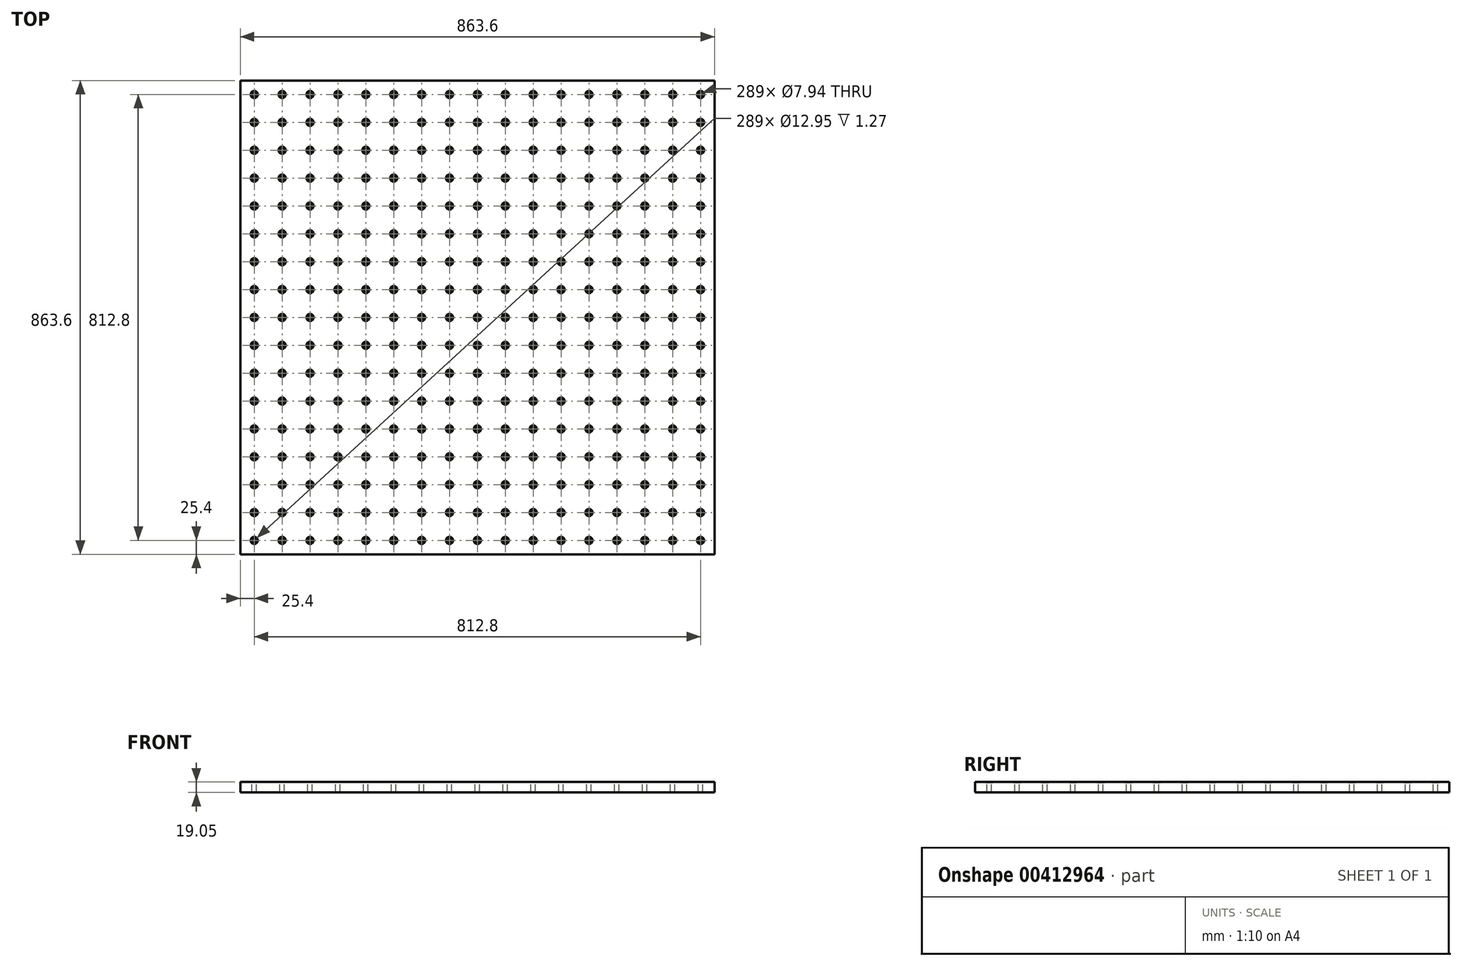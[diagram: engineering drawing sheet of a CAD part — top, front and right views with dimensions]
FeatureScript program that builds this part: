
annotation { "Feature Type Name" : "Feature", "Feature Type Description" : "" }
export const myFeature = defineFeature(function(context is Context, id is Id, definition is map)
    precondition{}
    {
        {
            var Q0;
            Q0=qCreatedBy(makeId("Top.planeOp"),FACE);
            var sketch = newSketch(context, id + "F0", { "sketchPlane" : qUnion([Q0])});
            skLineSegment(sketch, "E0.bottom", {"start": v(431.8, -431.8) * mm, "end": v(-431.8, -431.8) * mm});
            skLineSegment(sketch, "E0.top", {"start": v(431.8, 431.8) * mm, "end": v(-431.8, 431.8) * mm});
            skLineSegment(sketch, "E0.left", {"start": v(431.8, -431.8) * mm, "end": v(431.8, 431.8) * mm});
            skLineSegment(sketch, "E0.right", {"start": v(-431.8, -431.8) * mm, "end": v(-431.8, 431.8) * mm});
            skPoint(sketch, "E0.middle", {"position": v(0, 0) * mm});
            skSolve(sketch);
        }
        {
            var Q0;
            Q0=makeQuery(id+"F0.imprint","IMPRINT",FACE,{"disambiguationData":[TD([[makeQuery(id+"F0.imprint","IMPRINT",EDGE,{"derivedFrom":sQuery(id+"F0.wireOp",EDGE,"E0.bottom")}),-1.0]])]});
            extrude(context, id + "F1", {"entities" : qUnion([Q0]), "depth" : 19.05 * mm});
        }
        {
            var Q0;
            Q0=makeQuery(id+"F1.opExtrude","CAP_FACE",FACE,{"disambiguationData":[OSD([sQuery(id+"F0.wireOp",EDGE,"E0.bottom"),sQuery(id+"F0.wireOp",EDGE,"E0.top"),sQuery(id+"F0.wireOp",EDGE,"E0.left"),sQuery(id+"F0.wireOp",EDGE,"E0.right")])],"isStart":false});
            var sketch = newSketch(context, id + "F2", { "sketchPlane" : qUnion([Q0])});
            skLineSegment(sketch, "E1.bottom", {"start": v(406.4, -406.4) * mm, "end": v(-406.4, -406.4) * mm, "construction": true});
            skLineSegment(sketch, "E1.top", {"start": v(406.4, 406.4) * mm, "end": v(-406.4, 406.4) * mm, "construction": true});
            skLineSegment(sketch, "E1.left", {"start": v(406.4, -406.4) * mm, "end": v(406.4, 406.4) * mm, "construction": true});
            skLineSegment(sketch, "E1.right", {"start": v(-406.4, -406.4) * mm, "end": v(-406.4, 406.4) * mm, "construction": true});
            skPoint(sketch, "E1.middle", {"position": v(0, 0) * mm});
            skPoint(sketch, "E2", {"position": v(-406.4, -406.4) * mm});
            skPoint(sketch, "E3.0.1.0", {"position": v(-406.4, -355.6) * mm});
            skPoint(sketch, "E3.0.2.0", {"position": v(-406.4, -304.8) * mm});
            skPoint(sketch, "E3.0.3.0", {"position": v(-406.4, -254) * mm});
            skPoint(sketch, "E3.0.4.0", {"position": v(-406.4, -203.2) * mm});
            skPoint(sketch, "E3.0.5.0", {"position": v(-406.4, -152.4) * mm});
            skPoint(sketch, "E3.0.6.0", {"position": v(-406.4, -101.6) * mm});
            skPoint(sketch, "E3.0.7.0", {"position": v(-406.4, -50.8) * mm});
            skPoint(sketch, "E3.0.8.0", {"position": v(-406.4, 0) * mm});
            skPoint(sketch, "E3.0.9.0", {"position": v(-406.4, 50.8) * mm});
            skPoint(sketch, "E3.0.10.0", {"position": v(-406.4, 101.6) * mm});
            skPoint(sketch, "E3.0.11.0", {"position": v(-406.4, 152.4) * mm});
            skPoint(sketch, "E3.0.12.0", {"position": v(-406.4, 203.2) * mm});
            skPoint(sketch, "E3.0.13.0", {"position": v(-406.4, 254) * mm});
            skPoint(sketch, "E3.0.14.0", {"position": v(-406.4, 304.8) * mm});
            skPoint(sketch, "E3.0.15.0", {"position": v(-406.4, 355.6) * mm});
            skPoint(sketch, "E3.0.16.0", {"position": v(-406.4, 406.4) * mm});
            skPoint(sketch, "E3.1.0.0", {"position": v(-355.6, -406.4) * mm});
            skPoint(sketch, "E3.1.1.0", {"position": v(-355.6, -355.6) * mm});
            skPoint(sketch, "E3.1.2.0", {"position": v(-355.6, -304.8) * mm});
            skPoint(sketch, "E3.1.3.0", {"position": v(-355.6, -254) * mm});
            skPoint(sketch, "E3.1.4.0", {"position": v(-355.6, -203.2) * mm});
            skPoint(sketch, "E3.1.5.0", {"position": v(-355.6, -152.4) * mm});
            skPoint(sketch, "E3.1.6.0", {"position": v(-355.6, -101.6) * mm});
            skPoint(sketch, "E3.1.7.0", {"position": v(-355.6, -50.8) * mm});
            skPoint(sketch, "E3.1.8.0", {"position": v(-355.6, 0) * mm});
            skPoint(sketch, "E3.1.9.0", {"position": v(-355.6, 50.8) * mm});
            skPoint(sketch, "E3.1.10.0", {"position": v(-355.6, 101.6) * mm});
            skPoint(sketch, "E3.1.11.0", {"position": v(-355.6, 152.4) * mm});
            skPoint(sketch, "E3.1.12.0", {"position": v(-355.6, 203.2) * mm});
            skPoint(sketch, "E3.1.13.0", {"position": v(-355.6, 254) * mm});
            skPoint(sketch, "E3.1.14.0", {"position": v(-355.6, 304.8) * mm});
            skPoint(sketch, "E3.1.15.0", {"position": v(-355.6, 355.6) * mm});
            skPoint(sketch, "E3.1.16.0", {"position": v(-355.6, 406.4) * mm});
            skPoint(sketch, "E3.2.0.0", {"position": v(-304.8, -406.4) * mm});
            skPoint(sketch, "E3.2.1.0", {"position": v(-304.8, -355.6) * mm});
            skPoint(sketch, "E3.2.2.0", {"position": v(-304.8, -304.8) * mm});
            skPoint(sketch, "E3.2.3.0", {"position": v(-304.8, -254) * mm});
            skPoint(sketch, "E3.2.4.0", {"position": v(-304.8, -203.2) * mm});
            skPoint(sketch, "E3.2.5.0", {"position": v(-304.8, -152.4) * mm});
            skPoint(sketch, "E3.2.6.0", {"position": v(-304.8, -101.6) * mm});
            skPoint(sketch, "E3.2.7.0", {"position": v(-304.8, -50.8) * mm});
            skPoint(sketch, "E3.2.8.0", {"position": v(-304.8, 0) * mm});
            skPoint(sketch, "E3.2.9.0", {"position": v(-304.8, 50.8) * mm});
            skPoint(sketch, "E3.2.10.0", {"position": v(-304.8, 101.6) * mm});
            skPoint(sketch, "E3.2.11.0", {"position": v(-304.8, 152.4) * mm});
            skPoint(sketch, "E3.2.12.0", {"position": v(-304.8, 203.2) * mm});
            skPoint(sketch, "E3.2.13.0", {"position": v(-304.8, 254) * mm});
            skPoint(sketch, "E3.2.14.0", {"position": v(-304.8, 304.8) * mm});
            skPoint(sketch, "E3.2.15.0", {"position": v(-304.8, 355.6) * mm});
            skPoint(sketch, "E3.2.16.0", {"position": v(-304.8, 406.4) * mm});
            skPoint(sketch, "E3.3.0.0", {"position": v(-254, -406.4) * mm});
            skPoint(sketch, "E3.3.1.0", {"position": v(-254, -355.6) * mm});
            skPoint(sketch, "E3.3.2.0", {"position": v(-254, -304.8) * mm});
            skPoint(sketch, "E3.3.3.0", {"position": v(-254, -254) * mm});
            skPoint(sketch, "E3.3.4.0", {"position": v(-254, -203.2) * mm});
            skPoint(sketch, "E3.3.5.0", {"position": v(-254, -152.4) * mm});
            skPoint(sketch, "E3.3.6.0", {"position": v(-254, -101.6) * mm});
            skPoint(sketch, "E3.3.7.0", {"position": v(-254, -50.8) * mm});
            skPoint(sketch, "E3.3.8.0", {"position": v(-254, 0) * mm});
            skPoint(sketch, "E3.3.9.0", {"position": v(-254, 50.8) * mm});
            skPoint(sketch, "E3.3.10.0", {"position": v(-254, 101.6) * mm});
            skPoint(sketch, "E3.3.11.0", {"position": v(-254, 152.4) * mm});
            skPoint(sketch, "E3.3.12.0", {"position": v(-254, 203.2) * mm});
            skPoint(sketch, "E3.3.13.0", {"position": v(-254, 254) * mm});
            skPoint(sketch, "E3.3.14.0", {"position": v(-254, 304.8) * mm});
            skPoint(sketch, "E3.3.15.0", {"position": v(-254, 355.6) * mm});
            skPoint(sketch, "E3.3.16.0", {"position": v(-254, 406.4) * mm});
            skPoint(sketch, "E3.4.0.0", {"position": v(-203.2, -406.4) * mm});
            skPoint(sketch, "E3.4.1.0", {"position": v(-203.2, -355.6) * mm});
            skPoint(sketch, "E3.4.2.0", {"position": v(-203.2, -304.8) * mm});
            skPoint(sketch, "E3.4.3.0", {"position": v(-203.2, -254) * mm});
            skPoint(sketch, "E3.4.4.0", {"position": v(-203.2, -203.2) * mm});
            skPoint(sketch, "E3.4.5.0", {"position": v(-203.2, -152.4) * mm});
            skPoint(sketch, "E3.4.6.0", {"position": v(-203.2, -101.6) * mm});
            skPoint(sketch, "E3.4.7.0", {"position": v(-203.2, -50.8) * mm});
            skPoint(sketch, "E3.4.8.0", {"position": v(-203.2, 0) * mm});
            skPoint(sketch, "E3.4.9.0", {"position": v(-203.2, 50.8) * mm});
            skPoint(sketch, "E3.4.10.0", {"position": v(-203.2, 101.6) * mm});
            skPoint(sketch, "E3.4.11.0", {"position": v(-203.2, 152.4) * mm});
            skPoint(sketch, "E3.4.12.0", {"position": v(-203.2, 203.2) * mm});
            skPoint(sketch, "E3.4.13.0", {"position": v(-203.2, 254) * mm});
            skPoint(sketch, "E3.4.14.0", {"position": v(-203.2, 304.8) * mm});
            skPoint(sketch, "E3.4.15.0", {"position": v(-203.2, 355.6) * mm});
            skPoint(sketch, "E3.4.16.0", {"position": v(-203.2, 406.4) * mm});
            skPoint(sketch, "E3.5.0.0", {"position": v(-152.4, -406.4) * mm});
            skPoint(sketch, "E3.5.1.0", {"position": v(-152.4, -355.6) * mm});
            skPoint(sketch, "E3.5.2.0", {"position": v(-152.4, -304.8) * mm});
            skPoint(sketch, "E3.5.3.0", {"position": v(-152.4, -254) * mm});
            skPoint(sketch, "E3.5.4.0", {"position": v(-152.4, -203.2) * mm});
            skPoint(sketch, "E3.5.5.0", {"position": v(-152.4, -152.4) * mm});
            skPoint(sketch, "E3.5.6.0", {"position": v(-152.4, -101.6) * mm});
            skPoint(sketch, "E3.5.7.0", {"position": v(-152.4, -50.8) * mm});
            skPoint(sketch, "E3.5.8.0", {"position": v(-152.4, 0) * mm});
            skPoint(sketch, "E3.5.9.0", {"position": v(-152.4, 50.8) * mm});
            skPoint(sketch, "E3.5.10.0", {"position": v(-152.4, 101.6) * mm});
            skPoint(sketch, "E3.5.11.0", {"position": v(-152.4, 152.4) * mm});
            skPoint(sketch, "E3.5.12.0", {"position": v(-152.4, 203.2) * mm});
            skPoint(sketch, "E3.5.13.0", {"position": v(-152.4, 254) * mm});
            skPoint(sketch, "E3.5.14.0", {"position": v(-152.4, 304.8) * mm});
            skPoint(sketch, "E3.5.15.0", {"position": v(-152.4, 355.6) * mm});
            skPoint(sketch, "E3.5.16.0", {"position": v(-152.4, 406.4) * mm});
            skPoint(sketch, "E3.6.0.0", {"position": v(-101.6, -406.4) * mm});
            skPoint(sketch, "E3.6.1.0", {"position": v(-101.6, -355.6) * mm});
            skPoint(sketch, "E3.6.2.0", {"position": v(-101.6, -304.8) * mm});
            skPoint(sketch, "E3.6.3.0", {"position": v(-101.6, -254) * mm});
            skPoint(sketch, "E3.6.4.0", {"position": v(-101.6, -203.2) * mm});
            skPoint(sketch, "E3.6.5.0", {"position": v(-101.6, -152.4) * mm});
            skPoint(sketch, "E3.6.6.0", {"position": v(-101.6, -101.6) * mm});
            skPoint(sketch, "E3.6.7.0", {"position": v(-101.6, -50.8) * mm});
            skPoint(sketch, "E3.6.8.0", {"position": v(-101.6, 0) * mm});
            skPoint(sketch, "E3.6.9.0", {"position": v(-101.6, 50.8) * mm});
            skPoint(sketch, "E3.6.10.0", {"position": v(-101.6, 101.6) * mm});
            skPoint(sketch, "E3.6.11.0", {"position": v(-101.6, 152.4) * mm});
            skPoint(sketch, "E3.6.12.0", {"position": v(-101.6, 203.2) * mm});
            skPoint(sketch, "E3.6.13.0", {"position": v(-101.6, 254) * mm});
            skPoint(sketch, "E3.6.14.0", {"position": v(-101.6, 304.8) * mm});
            skPoint(sketch, "E3.6.15.0", {"position": v(-101.6, 355.6) * mm});
            skPoint(sketch, "E3.6.16.0", {"position": v(-101.6, 406.4) * mm});
            skPoint(sketch, "E3.7.0.0", {"position": v(-50.8, -406.4) * mm});
            skPoint(sketch, "E3.7.1.0", {"position": v(-50.8, -355.6) * mm});
            skPoint(sketch, "E3.7.2.0", {"position": v(-50.8, -304.8) * mm});
            skPoint(sketch, "E3.7.3.0", {"position": v(-50.8, -254) * mm});
            skPoint(sketch, "E3.7.4.0", {"position": v(-50.8, -203.2) * mm});
            skPoint(sketch, "E3.7.5.0", {"position": v(-50.8, -152.4) * mm});
            skPoint(sketch, "E3.7.6.0", {"position": v(-50.8, -101.6) * mm});
            skPoint(sketch, "E3.7.7.0", {"position": v(-50.8, -50.8) * mm});
            skPoint(sketch, "E3.7.8.0", {"position": v(-50.8, 0) * mm});
            skPoint(sketch, "E3.7.9.0", {"position": v(-50.8, 50.8) * mm});
            skPoint(sketch, "E3.7.10.0", {"position": v(-50.8, 101.6) * mm});
            skPoint(sketch, "E3.7.11.0", {"position": v(-50.8, 152.4) * mm});
            skPoint(sketch, "E3.7.12.0", {"position": v(-50.8, 203.2) * mm});
            skPoint(sketch, "E3.7.13.0", {"position": v(-50.8, 254) * mm});
            skPoint(sketch, "E3.7.14.0", {"position": v(-50.8, 304.8) * mm});
            skPoint(sketch, "E3.7.15.0", {"position": v(-50.8, 355.6) * mm});
            skPoint(sketch, "E3.7.16.0", {"position": v(-50.8, 406.4) * mm});
            skPoint(sketch, "E3.8.0.0", {"position": v(0, -406.4) * mm});
            skPoint(sketch, "E3.8.1.0", {"position": v(0, -355.6) * mm});
            skPoint(sketch, "E3.8.2.0", {"position": v(0, -304.8) * mm});
            skPoint(sketch, "E3.8.3.0", {"position": v(0, -254) * mm});
            skPoint(sketch, "E3.8.4.0", {"position": v(0, -203.2) * mm});
            skPoint(sketch, "E3.8.5.0", {"position": v(0, -152.4) * mm});
            skPoint(sketch, "E3.8.6.0", {"position": v(0, -101.6) * mm});
            skPoint(sketch, "E3.8.7.0", {"position": v(0, -50.8) * mm});
            skPoint(sketch, "E3.8.9.0", {"position": v(0, 50.8) * mm});
            skPoint(sketch, "E3.8.10.0", {"position": v(0, 101.6) * mm});
            skPoint(sketch, "E3.8.11.0", {"position": v(0, 152.4) * mm});
            skPoint(sketch, "E3.8.12.0", {"position": v(0, 203.2) * mm});
            skPoint(sketch, "E3.8.13.0", {"position": v(0, 254) * mm});
            skPoint(sketch, "E3.8.14.0", {"position": v(0, 304.8) * mm});
            skPoint(sketch, "E3.8.15.0", {"position": v(0, 355.6) * mm});
            skPoint(sketch, "E3.8.16.0", {"position": v(0, 406.4) * mm});
            skPoint(sketch, "E3.9.0.0", {"position": v(50.8, -406.4) * mm});
            skPoint(sketch, "E3.9.1.0", {"position": v(50.8, -355.6) * mm});
            skPoint(sketch, "E3.9.2.0", {"position": v(50.8, -304.8) * mm});
            skPoint(sketch, "E3.9.3.0", {"position": v(50.8, -254) * mm});
            skPoint(sketch, "E3.9.4.0", {"position": v(50.8, -203.2) * mm});
            skPoint(sketch, "E3.9.5.0", {"position": v(50.8, -152.4) * mm});
            skPoint(sketch, "E3.9.6.0", {"position": v(50.8, -101.6) * mm});
            skPoint(sketch, "E3.9.7.0", {"position": v(50.8, -50.8) * mm});
            skPoint(sketch, "E3.9.8.0", {"position": v(50.8, 0) * mm});
            skPoint(sketch, "E3.9.9.0", {"position": v(50.8, 50.8) * mm});
            skPoint(sketch, "E3.9.10.0", {"position": v(50.8, 101.6) * mm});
            skPoint(sketch, "E3.9.11.0", {"position": v(50.8, 152.4) * mm});
            skPoint(sketch, "E3.9.12.0", {"position": v(50.8, 203.2) * mm});
            skPoint(sketch, "E3.9.13.0", {"position": v(50.8, 254) * mm});
            skPoint(sketch, "E3.9.14.0", {"position": v(50.8, 304.8) * mm});
            skPoint(sketch, "E3.9.15.0", {"position": v(50.8, 355.6) * mm});
            skPoint(sketch, "E3.9.16.0", {"position": v(50.8, 406.4) * mm});
            skPoint(sketch, "E3.10.0.0", {"position": v(101.6, -406.4) * mm});
            skPoint(sketch, "E3.10.1.0", {"position": v(101.6, -355.6) * mm});
            skPoint(sketch, "E3.10.2.0", {"position": v(101.6, -304.8) * mm});
            skPoint(sketch, "E3.10.3.0", {"position": v(101.6, -254) * mm});
            skPoint(sketch, "E3.10.4.0", {"position": v(101.6, -203.2) * mm});
            skPoint(sketch, "E3.10.5.0", {"position": v(101.6, -152.4) * mm});
            skPoint(sketch, "E3.10.6.0", {"position": v(101.6, -101.6) * mm});
            skPoint(sketch, "E3.10.7.0", {"position": v(101.6, -50.8) * mm});
            skPoint(sketch, "E3.10.8.0", {"position": v(101.6, 0) * mm});
            skPoint(sketch, "E3.10.9.0", {"position": v(101.6, 50.8) * mm});
            skPoint(sketch, "E3.10.10.0", {"position": v(101.6, 101.6) * mm});
            skPoint(sketch, "E3.10.11.0", {"position": v(101.6, 152.4) * mm});
            skPoint(sketch, "E3.10.12.0", {"position": v(101.6, 203.2) * mm});
            skPoint(sketch, "E3.10.13.0", {"position": v(101.6, 254) * mm});
            skPoint(sketch, "E3.10.14.0", {"position": v(101.6, 304.8) * mm});
            skPoint(sketch, "E3.10.15.0", {"position": v(101.6, 355.6) * mm});
            skPoint(sketch, "E3.10.16.0", {"position": v(101.6, 406.4) * mm});
            skPoint(sketch, "E3.11.0.0", {"position": v(152.4, -406.4) * mm});
            skPoint(sketch, "E3.11.1.0", {"position": v(152.4, -355.6) * mm});
            skPoint(sketch, "E3.11.2.0", {"position": v(152.4, -304.8) * mm});
            skPoint(sketch, "E3.11.3.0", {"position": v(152.4, -254) * mm});
            skPoint(sketch, "E3.11.4.0", {"position": v(152.4, -203.2) * mm});
            skPoint(sketch, "E3.11.5.0", {"position": v(152.4, -152.4) * mm});
            skPoint(sketch, "E3.11.6.0", {"position": v(152.4, -101.6) * mm});
            skPoint(sketch, "E3.11.7.0", {"position": v(152.4, -50.8) * mm});
            skPoint(sketch, "E3.11.8.0", {"position": v(152.4, 0) * mm});
            skPoint(sketch, "E3.11.9.0", {"position": v(152.4, 50.8) * mm});
            skPoint(sketch, "E3.11.10.0", {"position": v(152.4, 101.6) * mm});
            skPoint(sketch, "E3.11.11.0", {"position": v(152.4, 152.4) * mm});
            skPoint(sketch, "E3.11.12.0", {"position": v(152.4, 203.2) * mm});
            skPoint(sketch, "E3.11.13.0", {"position": v(152.4, 254) * mm});
            skPoint(sketch, "E3.11.14.0", {"position": v(152.4, 304.8) * mm});
            skPoint(sketch, "E3.11.15.0", {"position": v(152.4, 355.6) * mm});
            skPoint(sketch, "E3.11.16.0", {"position": v(152.4, 406.4) * mm});
            skPoint(sketch, "E3.12.0.0", {"position": v(203.2, -406.4) * mm});
            skPoint(sketch, "E3.12.1.0", {"position": v(203.2, -355.6) * mm});
            skPoint(sketch, "E3.12.2.0", {"position": v(203.2, -304.8) * mm});
            skPoint(sketch, "E3.12.3.0", {"position": v(203.2, -254) * mm});
            skPoint(sketch, "E3.12.4.0", {"position": v(203.2, -203.2) * mm});
            skPoint(sketch, "E3.12.5.0", {"position": v(203.2, -152.4) * mm});
            skPoint(sketch, "E3.12.6.0", {"position": v(203.2, -101.6) * mm});
            skPoint(sketch, "E3.12.7.0", {"position": v(203.2, -50.8) * mm});
            skPoint(sketch, "E3.12.8.0", {"position": v(203.2, 0) * mm});
            skPoint(sketch, "E3.12.9.0", {"position": v(203.2, 50.8) * mm});
            skPoint(sketch, "E3.12.10.0", {"position": v(203.2, 101.6) * mm});
            skPoint(sketch, "E3.12.11.0", {"position": v(203.2, 152.4) * mm});
            skPoint(sketch, "E3.12.12.0", {"position": v(203.2, 203.2) * mm});
            skPoint(sketch, "E3.12.13.0", {"position": v(203.2, 254) * mm});
            skPoint(sketch, "E3.12.14.0", {"position": v(203.2, 304.8) * mm});
            skPoint(sketch, "E3.12.15.0", {"position": v(203.2, 355.6) * mm});
            skPoint(sketch, "E3.12.16.0", {"position": v(203.2, 406.4) * mm});
            skPoint(sketch, "E3.13.0.0", {"position": v(254, -406.4) * mm});
            skPoint(sketch, "E3.13.1.0", {"position": v(254, -355.6) * mm});
            skPoint(sketch, "E3.13.2.0", {"position": v(254, -304.8) * mm});
            skPoint(sketch, "E3.13.3.0", {"position": v(254, -254) * mm});
            skPoint(sketch, "E3.13.4.0", {"position": v(254, -203.2) * mm});
            skPoint(sketch, "E3.13.5.0", {"position": v(254, -152.4) * mm});
            skPoint(sketch, "E3.13.6.0", {"position": v(254, -101.6) * mm});
            skPoint(sketch, "E3.13.7.0", {"position": v(254, -50.8) * mm});
            skPoint(sketch, "E3.13.8.0", {"position": v(254, 0) * mm});
            skPoint(sketch, "E3.13.9.0", {"position": v(254, 50.8) * mm});
            skPoint(sketch, "E3.13.10.0", {"position": v(254, 101.6) * mm});
            skPoint(sketch, "E3.13.11.0", {"position": v(254, 152.4) * mm});
            skPoint(sketch, "E3.13.12.0", {"position": v(254, 203.2) * mm});
            skPoint(sketch, "E3.13.13.0", {"position": v(254, 254) * mm});
            skPoint(sketch, "E3.13.14.0", {"position": v(254, 304.8) * mm});
            skPoint(sketch, "E3.13.15.0", {"position": v(254, 355.6) * mm});
            skPoint(sketch, "E3.13.16.0", {"position": v(254, 406.4) * mm});
            skPoint(sketch, "E3.14.0.0", {"position": v(304.8, -406.4) * mm});
            skPoint(sketch, "E3.14.1.0", {"position": v(304.8, -355.6) * mm});
            skPoint(sketch, "E3.14.2.0", {"position": v(304.8, -304.8) * mm});
            skPoint(sketch, "E3.14.3.0", {"position": v(304.8, -254) * mm});
            skPoint(sketch, "E3.14.4.0", {"position": v(304.8, -203.2) * mm});
            skPoint(sketch, "E3.14.5.0", {"position": v(304.8, -152.4) * mm});
            skPoint(sketch, "E3.14.6.0", {"position": v(304.8, -101.6) * mm});
            skPoint(sketch, "E3.14.7.0", {"position": v(304.8, -50.8) * mm});
            skPoint(sketch, "E3.14.8.0", {"position": v(304.8, 0) * mm});
            skPoint(sketch, "E3.14.9.0", {"position": v(304.8, 50.8) * mm});
            skPoint(sketch, "E3.14.10.0", {"position": v(304.8, 101.6) * mm});
            skPoint(sketch, "E3.14.11.0", {"position": v(304.8, 152.4) * mm});
            skPoint(sketch, "E3.14.12.0", {"position": v(304.8, 203.2) * mm});
            skPoint(sketch, "E3.14.13.0", {"position": v(304.8, 254) * mm});
            skPoint(sketch, "E3.14.14.0", {"position": v(304.8, 304.8) * mm});
            skPoint(sketch, "E3.14.15.0", {"position": v(304.8, 355.6) * mm});
            skPoint(sketch, "E3.14.16.0", {"position": v(304.8, 406.4) * mm});
            skPoint(sketch, "E3.15.0.0", {"position": v(355.6, -406.4) * mm});
            skPoint(sketch, "E3.15.1.0", {"position": v(355.6, -355.6) * mm});
            skPoint(sketch, "E3.15.2.0", {"position": v(355.6, -304.8) * mm});
            skPoint(sketch, "E3.15.3.0", {"position": v(355.6, -254) * mm});
            skPoint(sketch, "E3.15.4.0", {"position": v(355.6, -203.2) * mm});
            skPoint(sketch, "E3.15.5.0", {"position": v(355.6, -152.4) * mm});
            skPoint(sketch, "E3.15.6.0", {"position": v(355.6, -101.6) * mm});
            skPoint(sketch, "E3.15.7.0", {"position": v(355.6, -50.8) * mm});
            skPoint(sketch, "E3.15.8.0", {"position": v(355.6, 0) * mm});
            skPoint(sketch, "E3.15.9.0", {"position": v(355.6, 50.8) * mm});
            skPoint(sketch, "E3.15.10.0", {"position": v(355.6, 101.6) * mm});
            skPoint(sketch, "E3.15.11.0", {"position": v(355.6, 152.4) * mm});
            skPoint(sketch, "E3.15.12.0", {"position": v(355.6, 203.2) * mm});
            skPoint(sketch, "E3.15.13.0", {"position": v(355.6, 254) * mm});
            skPoint(sketch, "E3.15.14.0", {"position": v(355.6, 304.8) * mm});
            skPoint(sketch, "E3.15.15.0", {"position": v(355.6, 355.6) * mm});
            skPoint(sketch, "E3.15.16.0", {"position": v(355.6, 406.4) * mm});
            skPoint(sketch, "E3.16.0.0", {"position": v(406.4, -406.4) * mm});
            skPoint(sketch, "E3.16.1.0", {"position": v(406.4, -355.6) * mm});
            skPoint(sketch, "E3.16.2.0", {"position": v(406.4, -304.8) * mm});
            skPoint(sketch, "E3.16.3.0", {"position": v(406.4, -254) * mm});
            skPoint(sketch, "E3.16.4.0", {"position": v(406.4, -203.2) * mm});
            skPoint(sketch, "E3.16.5.0", {"position": v(406.4, -152.4) * mm});
            skPoint(sketch, "E3.16.6.0", {"position": v(406.4, -101.6) * mm});
            skPoint(sketch, "E3.16.7.0", {"position": v(406.4, -50.8) * mm});
            skPoint(sketch, "E3.16.8.0", {"position": v(406.4, 0) * mm});
            skPoint(sketch, "E3.16.9.0", {"position": v(406.4, 50.8) * mm});
            skPoint(sketch, "E3.16.10.0", {"position": v(406.4, 101.6) * mm});
            skPoint(sketch, "E3.16.11.0", {"position": v(406.4, 152.4) * mm});
            skPoint(sketch, "E3.16.12.0", {"position": v(406.4, 203.2) * mm});
            skPoint(sketch, "E3.16.13.0", {"position": v(406.4, 254) * mm});
            skPoint(sketch, "E3.16.14.0", {"position": v(406.4, 304.8) * mm});
            skPoint(sketch, "E3.16.15.0", {"position": v(406.4, 355.6) * mm});
            skPoint(sketch, "E3.16.16.0", {"position": v(406.4, 406.4) * mm});
            skLineSegment(sketch, "E3.direction1", {"start": v(-406.4, -406.4) * mm, "end": v(-355.6, -406.4) * mm, "construction": true});
            skLineSegment(sketch, "E3.direction2", {"start": v(-406.4, -406.4) * mm, "end": v(-406.4, -355.6) * mm, "construction": true});
            skSolve(sketch);
        }
        {
            var Q0;
            Q0=sQuery(id+"F2.wireOp",VERTEX,"E3.4.6.0");
            var Q1;
            Q1=sQuery(id+"F2.wireOp",VERTEX,"E3.3.7.0");
            var Q2;
            Q2=sQuery(id+"F2.wireOp",VERTEX,"E3.3.16.0");
            var Q3;
            Q3=sQuery(id+"F2.wireOp",VERTEX,"E3.3.0.0");
            var Q4;
            Q4=sQuery(id+"F2.wireOp",VERTEX,"E3.2.1.0");
            var Q5;
            Q5=sQuery(id+"F2.wireOp",VERTEX,"E3.1.2.0");
            var Q6;
            Q6=sQuery(id+"F2.wireOp",VERTEX,"E3.4.15.0");
            var Q7;
            Q7=sQuery(id+"F2.wireOp",VERTEX,"E3.2.12.0");
            var Q8;
            Q8=sQuery(id+"F2.wireOp",VERTEX,"E3.1.13.0");
            var Q9;
            Q9=sQuery(id+"F2.wireOp",VERTEX,"E3.0.14.0");
            var Q10;
            Q10=sQuery(id+"F2.wireOp",VERTEX,"E3.4.10.0");
            var Q11;
            Q11=sQuery(id+"F2.wireOp",VERTEX,"E3.3.11.0");
            var Q12;
            Q12=sQuery(id+"F2.wireOp",VERTEX,"E3.2.8.0");
            var Q13;
            Q13=sQuery(id+"F2.wireOp",VERTEX,"E3.1.9.0");
            var Q14;
            Q14=sQuery(id+"F2.wireOp",VERTEX,"E3.0.10.0");
            var Q15;
            Q15=sQuery(id+"F2.wireOp",VERTEX,"E3.0.8.0");
            var Q16;
            Q16=sQuery(id+"F2.wireOp",VERTEX,"E3.4.4.0");
            var Q17;
            Q17=sQuery(id+"F2.wireOp",VERTEX,"E3.3.14.0");
            var Q18;
            Q18=sQuery(id+"F2.wireOp",VERTEX,"E3.3.5.0");
            var Q19;
            Q19=sQuery(id+"F2.wireOp",VERTEX,"E3.2.15.0");
            var Q20;
            Q20=sQuery(id+"F2.wireOp",VERTEX,"E3.1.16.0");
            var Q21;
            Q21=sQuery(id+"F2.wireOp",VERTEX,"E3.2.6.0");
            var Q22;
            Q22=sQuery(id+"F2.wireOp",VERTEX,"E3.1.7.0");
            var Q23;
            Q23=sQuery(id+"F2.wireOp",VERTEX,"E3.1.0.0");
            var Q24;
            Q24=sQuery(id+"F2.wireOp",VERTEX,"E3.4.13.0");
            var Q25;
            Q25=sQuery(id+"F2.wireOp",VERTEX,"E3.0.4.0");
            var Q26;
            Q26=sQuery(id+"F2.wireOp",VERTEX,"E3.4.0.0");
            var Q27;
            Q27=sQuery(id+"F2.wireOp",VERTEX,"E3.3.1.0");
            var Q28;
            Q28=sQuery(id+"F2.wireOp",VERTEX,"E3.2.2.0");
            var Q29;
            Q29=sQuery(id+"F2.wireOp",VERTEX,"E3.1.3.0");
            var Q30;
            Q30=sQuery(id+"F2.wireOp",VERTEX,"E3.4.16.0");
            var Q31;
            Q31=sQuery(id+"F2.wireOp",VERTEX,"E3.2.13.0");
            var Q32;
            Q32=sQuery(id+"F2.wireOp",VERTEX,"E3.1.14.0");
            var Q33;
            Q33=sQuery(id+"F2.wireOp",VERTEX,"E3.0.15.0");
            var Q34;
            Q34=sQuery(id+"F2.wireOp",VERTEX,"E3.4.11.0");
            var Q35;
            Q35=sQuery(id+"F2.wireOp",VERTEX,"E3.3.12.0");
            var Q36;
            Q36=sQuery(id+"F2.wireOp",VERTEX,"E3.2.9.0");
            var Q37;
            Q37=sQuery(id+"F2.wireOp",VERTEX,"E3.1.10.0");
            var Q38;
            Q38=sQuery(id+"F2.wireOp",VERTEX,"E3.0.11.0");
            var Q39;
            Q39=sQuery(id+"F2.wireOp",VERTEX,"E3.4.7.0");
            var Q40;
            Q40=sQuery(id+"F2.wireOp",VERTEX,"E3.3.8.0");
            var Q41;
            Q41=sQuery(id+"F2.wireOp",VERTEX,"E3.0.9.0");
            var Q42;
            Q42=sQuery(id+"F2.wireOp",VERTEX,"E3.3.15.0");
            var Q43;
            Q43=sQuery(id+"F2.wireOp",VERTEX,"E3.4.5.0");
            var Q44;
            Q44=sQuery(id+"F2.wireOp",VERTEX,"E3.3.6.0");
            var Q45;
            Q45=sQuery(id+"F2.wireOp",VERTEX,"E3.2.16.0");
            var Q46;
            Q46=sQuery(id+"F2.wireOp",VERTEX,"E3.2.7.0");
            var Q47;
            Q47=sQuery(id+"F2.wireOp",VERTEX,"E3.2.0.0");
            var Q48;
            Q48=sQuery(id+"F2.wireOp",VERTEX,"E3.1.8.0");
            var Q49;
            Q49=sQuery(id+"F2.wireOp",VERTEX,"E3.1.1.0");
            var Q50;
            Q50=sQuery(id+"F2.wireOp",VERTEX,"E3.4.14.0");
            var Q51;
            Q51=sQuery(id+"F2.wireOp",VERTEX,"E2");
            var Q52;
            Q52=sQuery(id+"F2.wireOp",VERTEX,"E3.0.5.0");
            var Q53;
            Q53=sQuery(id+"F2.wireOp",VERTEX,"E3.0.1.0");
            var Q54;
            Q54=sQuery(id+"F2.wireOp",VERTEX,"E3.4.1.0");
            var Q55;
            Q55=sQuery(id+"F2.wireOp",VERTEX,"E3.0.2.0");
            var Q56;
            Q56=sQuery(id+"F2.wireOp",VERTEX,"E3.3.2.0");
            var Q57;
            Q57=sQuery(id+"F2.wireOp",VERTEX,"E3.2.3.0");
            var Q58;
            Q58=sQuery(id+"F2.wireOp",VERTEX,"E3.1.4.0");
            var Q59;
            Q59=sQuery(id+"F2.wireOp",VERTEX,"E1.right.end");
            var Q60;
            Q60=sQuery(id+"F2.wireOp",VERTEX,"E3.2.10.0");
            var Q61;
            Q61=sQuery(id+"F2.wireOp",VERTEX,"E3.1.11.0");
            var Q62;
            Q62=sQuery(id+"F2.wireOp",VERTEX,"E3.0.12.0");
            var Q63;
            Q63=sQuery(id+"F2.wireOp",VERTEX,"E3.4.8.0");
            var Q64;
            Q64=sQuery(id+"F2.wireOp",VERTEX,"E3.3.9.0");
            var Q65;
            Q65=sQuery(id+"F2.wireOp",VERTEX,"E3.0.6.0");
            var Q66;
            Q66=sQuery(id+"F2.wireOp",VERTEX,"E3.4.2.0");
            var Q67;
            Q67=sQuery(id+"F2.wireOp",VERTEX,"E3.3.3.0");
            var Q68;
            Q68=sQuery(id+"F2.wireOp",VERTEX,"E3.2.4.0");
            var Q69;
            Q69=sQuery(id+"F2.wireOp",VERTEX,"E3.1.5.0");
            var Q70;
            Q70=sQuery(id+"F2.wireOp",VERTEX,"E3.2.11.0");
            var Q71;
            Q71=sQuery(id+"F2.wireOp",VERTEX,"E3.1.12.0");
            var Q72;
            Q72=sQuery(id+"F2.wireOp",VERTEX,"E3.0.13.0");
            var Q73;
            Q73=sQuery(id+"F2.wireOp",VERTEX,"E3.4.9.0");
            var Q74;
            Q74=sQuery(id+"F2.wireOp",VERTEX,"E3.3.10.0");
            var Q75;
            Q75=sQuery(id+"F2.wireOp",VERTEX,"E3.0.7.0");
            var Q76;
            Q76=sQuery(id+"F2.wireOp",VERTEX,"E3.4.3.0");
            var Q77;
            Q77=sQuery(id+"F2.wireOp",VERTEX,"E3.3.13.0");
            var Q78;
            Q78=sQuery(id+"F2.wireOp",VERTEX,"E3.2.14.0");
            var Q79;
            Q79=sQuery(id+"F2.wireOp",VERTEX,"E3.3.4.0");
            var Q80;
            Q80=sQuery(id+"F2.wireOp",VERTEX,"E3.2.5.0");
            var Q81;
            Q81=sQuery(id+"F2.wireOp",VERTEX,"E3.1.15.0");
            var Q82;
            Q82=sQuery(id+"F2.wireOp",VERTEX,"E3.1.6.0");
            var Q83;
            Q83=sQuery(id+"F2.wireOp",VERTEX,"E3.4.12.0");
            var Q84;
            Q84=sQuery(id+"F2.wireOp",VERTEX,"E3.0.3.0");
            var Q85;
            Q85=makeQuery(id+"F1.opExtrude","SWEPT_BODY",BODY,{"disambiguationData":[OSD([sQuery(id+"F0.wireOp",EDGE,"E0.bottom"),sQuery(id+"F0.wireOp",EDGE,"E0.top"),sQuery(id+"F0.wireOp",EDGE,"E0.left"),sQuery(id+"F0.wireOp",EDGE,"E0.right")])]});
            hole(context, id + "F3", {"style" : HoleStyle.C_BORE, "endStyle" : HoleEndStyle.THROUGH, "holeDiameter" : 7.94 * mm, "cBoreDiameter" : 12.95 * mm, "cBoreDepth" : 1.27 * mm, "isTappedThrough" : true, "tappedDepth" : 12.7 * mm, "tapClearance" : 3, "locations" : qUnion([Q0, Q1, Q2, Q3, Q4, Q5, Q6, Q7, Q8, Q9, Q10, Q11, Q12, Q13, Q14, Q15, Q16, Q17, Q18, Q19, Q20, Q21, Q22, Q23, Q24, Q25, Q26, Q27, Q28, Q29, Q30, Q31, Q32, Q33, Q34, Q35, Q36, Q37, Q38, Q39, Q40, Q41, Q42, Q43, Q44, Q45, Q46, Q47, Q48, Q49, Q50, Q51, Q52, Q53, Q54, Q55, Q56, Q57, Q58, Q59, Q60, Q61, Q62, Q63, Q64, Q65, Q66, Q67, Q68, Q69, Q70, Q71, Q72, Q73, Q74, Q75, Q76, Q77, Q78, Q79, Q80, Q81, Q82, Q83, Q84]), "scope" : qUnion([Q85])});
        }
        {
            var Q0;
            Q0=sQuery(id+"F2.wireOp",VERTEX,"E3.8.13.0");
            var Q1;
            Q1=sQuery(id+"F2.wireOp",VERTEX,"E3.9.12.0");
            var Q2;
            Q2=sQuery(id+"F2.wireOp",VERTEX,"E3.5.0.0");
            var Q3;
            Q3=sQuery(id+"F2.wireOp",VERTEX,"E3.5.16.0");
            var Q4;
            Q4=sQuery(id+"F2.wireOp",VERTEX,"E3.6.15.0");
            var Q5;
            Q5=sQuery(id+"F2.wireOp",VERTEX,"E3.7.14.0");
            var Q6;
            Q6=sQuery(id+"F2.wireOp",VERTEX,"E3.5.6.0");
            var Q7;
            Q7=sQuery(id+"F2.wireOp",VERTEX,"E3.6.5.0");
            var Q8;
            Q8=sQuery(id+"F2.wireOp",VERTEX,"E1.middle");
            var Q9;
            Q9=sQuery(id+"F2.wireOp",VERTEX,"E3.9.7.0");
            var Q10;
            Q10=sQuery(id+"F2.wireOp",VERTEX,"E3.5.11.0");
            var Q11;
            Q11=sQuery(id+"F2.wireOp",VERTEX,"E3.6.10.0");
            var Q12;
            Q12=sQuery(id+"F2.wireOp",VERTEX,"E3.7.9.0");
            var Q13;
            Q13=sQuery(id+"F2.wireOp",VERTEX,"E3.8.15.0");
            var Q14;
            Q14=sQuery(id+"F2.wireOp",VERTEX,"E3.9.14.0");
            var Q15;
            Q15=sQuery(id+"F2.wireOp",VERTEX,"E3.7.6.0");
            var Q16;
            Q16=sQuery(id+"F2.wireOp",VERTEX,"E3.8.5.0");
            var Q17;
            Q17=sQuery(id+"F2.wireOp",VERTEX,"E3.9.4.0");
            var Q18;
            Q18=sQuery(id+"F2.wireOp",VERTEX,"E3.5.2.0");
            var Q19;
            Q19=sQuery(id+"F2.wireOp",VERTEX,"E3.6.1.0");
            var Q20;
            Q20=sQuery(id+"F2.wireOp",VERTEX,"E3.7.0.0");
            var Q21;
            Q21=sQuery(id+"F2.wireOp",VERTEX,"E3.7.16.0");
            var Q22;
            Q22=sQuery(id+"F2.wireOp",VERTEX,"E3.5.8.0");
            var Q23;
            Q23=sQuery(id+"F2.wireOp",VERTEX,"E3.6.7.0");
            var Q24;
            Q24=sQuery(id+"F2.wireOp",VERTEX,"E3.7.5.0");
            var Q25;
            Q25=sQuery(id+"F2.wireOp",VERTEX,"E3.8.4.0");
            var Q26;
            Q26=sQuery(id+"F2.wireOp",VERTEX,"E3.9.3.0");
            var Q27;
            Q27=sQuery(id+"F2.wireOp",VERTEX,"E3.8.12.0");
            var Q28;
            Q28=sQuery(id+"F2.wireOp",VERTEX,"E3.9.11.0");
            var Q29;
            Q29=sQuery(id+"F2.wireOp",VERTEX,"E3.5.15.0");
            var Q30;
            Q30=sQuery(id+"F2.wireOp",VERTEX,"E3.6.14.0");
            var Q31;
            Q31=sQuery(id+"F2.wireOp",VERTEX,"E3.7.13.0");
            var Q32;
            Q32=sQuery(id+"F2.wireOp",VERTEX,"E3.8.11.0");
            var Q33;
            Q33=sQuery(id+"F2.wireOp",VERTEX,"E3.9.10.0");
            var Q34;
            Q34=sQuery(id+"F2.wireOp",VERTEX,"E3.7.4.0");
            var Q35;
            Q35=sQuery(id+"F2.wireOp",VERTEX,"E3.8.3.0");
            var Q36;
            Q36=sQuery(id+"F2.wireOp",VERTEX,"E3.9.2.0");
            var Q37;
            Q37=sQuery(id+"F2.wireOp",VERTEX,"E3.5.14.0");
            var Q38;
            Q38=sQuery(id+"F2.wireOp",VERTEX,"E3.5.7.0");
            var Q39;
            Q39=sQuery(id+"F2.wireOp",VERTEX,"E3.6.6.0");
            var Q40;
            Q40=sQuery(id+"F2.wireOp",VERTEX,"E3.6.13.0");
            var Q41;
            Q41=sQuery(id+"F2.wireOp",VERTEX,"E3.7.12.0");
            var Q42;
            Q42=sQuery(id+"F2.wireOp",VERTEX,"E3.8.14.0");
            var Q43;
            Q43=sQuery(id+"F2.wireOp",VERTEX,"E3.9.13.0");
            var Q44;
            Q44=sQuery(id+"F2.wireOp",VERTEX,"E3.5.1.0");
            var Q45;
            Q45=sQuery(id+"F2.wireOp",VERTEX,"E3.6.0.0");
            var Q46;
            Q46=sQuery(id+"F2.wireOp",VERTEX,"E3.6.16.0");
            var Q47;
            Q47=sQuery(id+"F2.wireOp",VERTEX,"E3.7.15.0");
            var Q48;
            Q48=sQuery(id+"F2.wireOp",VERTEX,"E3.7.3.0");
            var Q49;
            Q49=sQuery(id+"F2.wireOp",VERTEX,"E3.8.2.0");
            var Q50;
            Q50=sQuery(id+"F2.wireOp",VERTEX,"E3.9.1.0");
            var Q51;
            Q51=sQuery(id+"F2.wireOp",VERTEX,"E3.8.10.0");
            var Q52;
            Q52=sQuery(id+"F2.wireOp",VERTEX,"E3.9.9.0");
            var Q53;
            Q53=sQuery(id+"F2.wireOp",VERTEX,"E3.5.13.0");
            var Q54;
            Q54=sQuery(id+"F2.wireOp",VERTEX,"E3.6.12.0");
            var Q55;
            Q55=sQuery(id+"F2.wireOp",VERTEX,"E3.7.11.0");
            var Q56;
            Q56=sQuery(id+"F2.wireOp",VERTEX,"E3.7.8.0");
            var Q57;
            Q57=sQuery(id+"F2.wireOp",VERTEX,"E3.8.7.0");
            var Q58;
            Q58=sQuery(id+"F2.wireOp",VERTEX,"E3.9.6.0");
            var Q59;
            Q59=sQuery(id+"F2.wireOp",VERTEX,"E3.5.5.0");
            var Q60;
            Q60=sQuery(id+"F2.wireOp",VERTEX,"E3.6.4.0");
            var Q61;
            Q61=sQuery(id+"F2.wireOp",VERTEX,"E3.5.10.0");
            var Q62;
            Q62=sQuery(id+"F2.wireOp",VERTEX,"E3.6.9.0");
            var Q63;
            Q63=sQuery(id+"F2.wireOp",VERTEX,"E3.9.0.0");
            var Q64;
            Q64=sQuery(id+"F2.wireOp",VERTEX,"E3.9.16.0");
            var Q65;
            Q65=sQuery(id+"F2.wireOp",VERTEX,"E3.5.4.0");
            var Q66;
            Q66=sQuery(id+"F2.wireOp",VERTEX,"E3.6.3.0");
            var Q67;
            Q67=sQuery(id+"F2.wireOp",VERTEX,"E3.7.2.0");
            var Q68;
            Q68=sQuery(id+"F2.wireOp",VERTEX,"E3.8.1.0");
            var Q69;
            Q69=sQuery(id+"F2.wireOp",VERTEX,"E3.8.9.0");
            var Q70;
            Q70=sQuery(id+"F2.wireOp",VERTEX,"E3.9.8.0");
            var Q71;
            Q71=sQuery(id+"F2.wireOp",VERTEX,"E3.5.12.0");
            var Q72;
            Q72=sQuery(id+"F2.wireOp",VERTEX,"E3.6.11.0");
            var Q73;
            Q73=sQuery(id+"F2.wireOp",VERTEX,"E3.7.10.0");
            var Q74;
            Q74=sQuery(id+"F2.wireOp",VERTEX,"E3.8.16.0");
            var Q75;
            Q75=sQuery(id+"F2.wireOp",VERTEX,"E3.9.15.0");
            var Q76;
            Q76=sQuery(id+"F2.wireOp",VERTEX,"E3.5.3.0");
            var Q77;
            Q77=sQuery(id+"F2.wireOp",VERTEX,"E3.7.7.0");
            var Q78;
            Q78=sQuery(id+"F2.wireOp",VERTEX,"E3.8.6.0");
            var Q79;
            Q79=sQuery(id+"F2.wireOp",VERTEX,"E3.6.2.0");
            var Q80;
            Q80=sQuery(id+"F2.wireOp",VERTEX,"E3.7.1.0");
            var Q81;
            Q81=sQuery(id+"F2.wireOp",VERTEX,"E3.9.5.0");
            var Q82;
            Q82=sQuery(id+"F2.wireOp",VERTEX,"E3.8.0.0");
            var Q83;
            Q83=sQuery(id+"F2.wireOp",VERTEX,"E3.5.9.0");
            var Q84;
            Q84=sQuery(id+"F2.wireOp",VERTEX,"E3.6.8.0");
            var Q85;
            Q85=makeQuery(id+"F1.opExtrude","SWEPT_BODY",BODY,{"disambiguationData":[OSD([sQuery(id+"F0.wireOp",EDGE,"E0.bottom"),sQuery(id+"F0.wireOp",EDGE,"E0.top"),sQuery(id+"F0.wireOp",EDGE,"E0.left"),sQuery(id+"F0.wireOp",EDGE,"E0.right")])]});
            hole(context, id + "F4", {"style" : HoleStyle.C_BORE, "endStyle" : HoleEndStyle.THROUGH, "holeDiameter" : 7.94 * mm, "cBoreDiameter" : 12.95 * mm, "cBoreDepth" : 1.27 * mm, "isTappedThrough" : true, "tappedDepth" : 12.7 * mm, "tapClearance" : 3, "locations" : qUnion([Q0, Q1, Q2, Q3, Q4, Q5, Q6, Q7, Q8, Q9, Q10, Q11, Q12, Q13, Q14, Q15, Q16, Q17, Q18, Q19, Q20, Q21, Q22, Q23, Q24, Q25, Q26, Q27, Q28, Q29, Q30, Q31, Q32, Q33, Q34, Q35, Q36, Q37, Q38, Q39, Q40, Q41, Q42, Q43, Q44, Q45, Q46, Q47, Q48, Q49, Q50, Q51, Q52, Q53, Q54, Q55, Q56, Q57, Q58, Q59, Q60, Q61, Q62, Q63, Q64, Q65, Q66, Q67, Q68, Q69, Q70, Q71, Q72, Q73, Q74, Q75, Q76, Q77, Q78, Q79, Q80, Q81, Q82, Q83, Q84]), "scope" : qUnion([Q85])});
        }
        {
            var Q0;
            Q0=sQuery(id+"F2.wireOp",VERTEX,"E3.10.11.0");
            var Q1;
            Q1=sQuery(id+"F2.wireOp",VERTEX,"E3.11.10.0");
            var Q2;
            Q2=sQuery(id+"F2.wireOp",VERTEX,"E3.12.8.0");
            var Q3;
            Q3=sQuery(id+"F2.wireOp",VERTEX,"E3.12.4.0");
            var Q4;
            Q4=sQuery(id+"F2.wireOp",VERTEX,"E3.13.3.0");
            var Q5;
            Q5=sQuery(id+"F2.wireOp",VERTEX,"E3.14.2.0");
            var Q6;
            Q6=sQuery(id+"F2.wireOp",VERTEX,"E3.10.6.0");
            var Q7;
            Q7=sQuery(id+"F2.wireOp",VERTEX,"E3.11.5.0");
            var Q8;
            Q8=sQuery(id+"F2.wireOp",VERTEX,"E3.14.13.0");
            var Q9;
            Q9=sQuery(id+"F2.wireOp",VERTEX,"E3.11.2.0");
            var Q10;
            Q10=sQuery(id+"F2.wireOp",VERTEX,"E3.13.7.0");
            var Q11;
            Q11=sQuery(id+"F2.wireOp",VERTEX,"E3.12.1.0");
            var Q12;
            Q12=sQuery(id+"F2.wireOp",VERTEX,"E3.14.6.0");
            var Q13;
            Q13=sQuery(id+"F2.wireOp",VERTEX,"E3.13.0.0");
            var Q14;
            Q14=sQuery(id+"F2.wireOp",VERTEX,"E3.13.16.0");
            var Q15;
            Q15=sQuery(id+"F2.wireOp",VERTEX,"E3.10.13.0");
            var Q16;
            Q16=sQuery(id+"F2.wireOp",VERTEX,"E3.11.12.0");
            var Q17;
            Q17=sQuery(id+"F2.wireOp",VERTEX,"E3.10.3.0");
            var Q18;
            Q18=sQuery(id+"F2.wireOp",VERTEX,"E3.14.15.0");
            var Q19;
            Q19=sQuery(id+"F2.wireOp",VERTEX,"E3.12.10.0");
            var Q20;
            Q20=sQuery(id+"F2.wireOp",VERTEX,"E3.13.9.0");
            var Q21;
            Q21=sQuery(id+"F2.wireOp",VERTEX,"E3.14.8.0");
            var Q22;
            Q22=sQuery(id+"F2.wireOp",VERTEX,"E3.11.0.0");
            var Q23;
            Q23=sQuery(id+"F2.wireOp",VERTEX,"E3.10.10.0");
            var Q24;
            Q24=sQuery(id+"F2.wireOp",VERTEX,"E3.11.9.0");
            var Q25;
            Q25=sQuery(id+"F2.wireOp",VERTEX,"E3.12.7.0");
            var Q26;
            Q26=sQuery(id+"F2.wireOp",VERTEX,"E3.13.6.0");
            var Q27;
            Q27=sQuery(id+"F2.wireOp",VERTEX,"E3.14.5.0");
            var Q28;
            Q28=sQuery(id+"F2.wireOp",VERTEX,"E3.10.9.0");
            var Q29;
            Q29=sQuery(id+"F2.wireOp",VERTEX,"E3.11.16.0");
            var Q30;
            Q30=sQuery(id+"F2.wireOp",VERTEX,"E3.12.15.0");
            var Q31;
            Q31=sQuery(id+"F2.wireOp",VERTEX,"E3.13.14.0");
            var Q32;
            Q32=sQuery(id+"F2.wireOp",VERTEX,"E3.11.8.0");
            var Q33;
            Q33=sQuery(id+"F2.wireOp",VERTEX,"E3.10.1.0");
            var Q34;
            Q34=sQuery(id+"F2.wireOp",VERTEX,"E3.10.2.0");
            var Q35;
            Q35=sQuery(id+"F2.wireOp",VERTEX,"E3.14.12.0");
            var Q36;
            Q36=sQuery(id+"F2.wireOp",VERTEX,"E3.14.14.0");
            var Q37;
            Q37=sQuery(id+"F2.wireOp",VERTEX,"E3.11.1.0");
            var Q38;
            Q38=sQuery(id+"F2.wireOp",VERTEX,"E3.12.0.0");
            var Q39;
            Q39=sQuery(id+"F2.wireOp",VERTEX,"E3.10.12.0");
            var Q40;
            Q40=sQuery(id+"F2.wireOp",VERTEX,"E3.11.11.0");
            var Q41;
            Q41=sQuery(id+"F2.wireOp",VERTEX,"E3.12.16.0");
            var Q42;
            Q42=sQuery(id+"F2.wireOp",VERTEX,"E3.13.15.0");
            var Q43;
            Q43=sQuery(id+"F2.wireOp",VERTEX,"E3.12.9.0");
            var Q44;
            Q44=sQuery(id+"F2.wireOp",VERTEX,"E3.13.8.0");
            var Q45;
            Q45=sQuery(id+"F2.wireOp",VERTEX,"E3.14.7.0");
            var Q46;
            Q46=sQuery(id+"F2.wireOp",VERTEX,"E3.10.16.0");
            var Q47;
            Q47=sQuery(id+"F2.wireOp",VERTEX,"E3.11.15.0");
            var Q48;
            Q48=sQuery(id+"F2.wireOp",VERTEX,"E3.12.14.0");
            var Q49;
            Q49=sQuery(id+"F2.wireOp",VERTEX,"E3.13.13.0");
            var Q50;
            Q50=sQuery(id+"F2.wireOp",VERTEX,"E3.10.0.0");
            var Q51;
            Q51=sQuery(id+"F2.wireOp",VERTEX,"E3.12.6.0");
            var Q52;
            Q52=sQuery(id+"F2.wireOp",VERTEX,"E3.13.5.0");
            var Q53;
            Q53=sQuery(id+"F2.wireOp",VERTEX,"E3.14.4.0");
            var Q54;
            Q54=sQuery(id+"F2.wireOp",VERTEX,"E3.10.8.0");
            var Q55;
            Q55=sQuery(id+"F2.wireOp",VERTEX,"E3.11.7.0");
            var Q56;
            Q56=sQuery(id+"F2.wireOp",VERTEX,"E3.11.4.0");
            var Q57;
            Q57=sQuery(id+"F2.wireOp",VERTEX,"E3.12.3.0");
            var Q58;
            Q58=sQuery(id+"F2.wireOp",VERTEX,"E3.13.2.0");
            var Q59;
            Q59=sQuery(id+"F2.wireOp",VERTEX,"E3.14.1.0");
            var Q60;
            Q60=sQuery(id+"F2.wireOp",VERTEX,"E3.12.13.0");
            var Q61;
            Q61=sQuery(id+"F2.wireOp",VERTEX,"E3.13.12.0");
            var Q62;
            Q62=sQuery(id+"F2.wireOp",VERTEX,"E3.14.11.0");
            var Q63;
            Q63=sQuery(id+"F2.wireOp",VERTEX,"E3.10.5.0");
            var Q64;
            Q64=sQuery(id+"F2.wireOp",VERTEX,"E3.12.5.0");
            var Q65;
            Q65=sQuery(id+"F2.wireOp",VERTEX,"E3.13.4.0");
            var Q66;
            Q66=sQuery(id+"F2.wireOp",VERTEX,"E3.10.15.0");
            var Q67;
            Q67=sQuery(id+"F2.wireOp",VERTEX,"E3.11.14.0");
            var Q68;
            Q68=sQuery(id+"F2.wireOp",VERTEX,"E3.14.3.0");
            var Q69;
            Q69=sQuery(id+"F2.wireOp",VERTEX,"E3.12.12.0");
            var Q70;
            Q70=sQuery(id+"F2.wireOp",VERTEX,"E3.13.11.0");
            var Q71;
            Q71=sQuery(id+"F2.wireOp",VERTEX,"E3.14.10.0");
            var Q72;
            Q72=sQuery(id+"F2.wireOp",VERTEX,"E3.10.7.0");
            var Q73;
            Q73=sQuery(id+"F2.wireOp",VERTEX,"E3.11.6.0");
            var Q74;
            Q74=sQuery(id+"F2.wireOp",VERTEX,"E3.14.16.0");
            var Q75;
            Q75=sQuery(id+"F2.wireOp",VERTEX,"E3.11.3.0");
            var Q76;
            Q76=sQuery(id+"F2.wireOp",VERTEX,"E3.12.2.0");
            var Q77;
            Q77=sQuery(id+"F2.wireOp",VERTEX,"E3.13.1.0");
            var Q78;
            Q78=sQuery(id+"F2.wireOp",VERTEX,"E3.10.14.0");
            var Q79;
            Q79=sQuery(id+"F2.wireOp",VERTEX,"E3.11.13.0");
            var Q80;
            Q80=sQuery(id+"F2.wireOp",VERTEX,"E3.14.0.0");
            var Q81;
            Q81=sQuery(id+"F2.wireOp",VERTEX,"E3.10.4.0");
            var Q82;
            Q82=sQuery(id+"F2.wireOp",VERTEX,"E3.12.11.0");
            var Q83;
            Q83=sQuery(id+"F2.wireOp",VERTEX,"E3.13.10.0");
            var Q84;
            Q84=sQuery(id+"F2.wireOp",VERTEX,"E3.14.9.0");
            var Q85;
            Q85=makeQuery(id+"F1.opExtrude","SWEPT_BODY",BODY,{"disambiguationData":[OSD([sQuery(id+"F0.wireOp",EDGE,"E0.bottom"),sQuery(id+"F0.wireOp",EDGE,"E0.top"),sQuery(id+"F0.wireOp",EDGE,"E0.left"),sQuery(id+"F0.wireOp",EDGE,"E0.right")])]});
            hole(context, id + "F5", {"style" : HoleStyle.C_BORE, "endStyle" : HoleEndStyle.THROUGH, "holeDiameter" : 7.94 * mm, "cBoreDiameter" : 12.95 * mm, "cBoreDepth" : 1.27 * mm, "isTappedThrough" : true, "tappedDepth" : 12.7 * mm, "tapClearance" : 3, "locations" : qUnion([Q0, Q1, Q2, Q3, Q4, Q5, Q6, Q7, Q8, Q9, Q10, Q11, Q12, Q13, Q14, Q15, Q16, Q17, Q18, Q19, Q20, Q21, Q22, Q23, Q24, Q25, Q26, Q27, Q28, Q29, Q30, Q31, Q32, Q33, Q34, Q35, Q36, Q37, Q38, Q39, Q40, Q41, Q42, Q43, Q44, Q45, Q46, Q47, Q48, Q49, Q50, Q51, Q52, Q53, Q54, Q55, Q56, Q57, Q58, Q59, Q60, Q61, Q62, Q63, Q64, Q65, Q66, Q67, Q68, Q69, Q70, Q71, Q72, Q73, Q74, Q75, Q76, Q77, Q78, Q79, Q80, Q81, Q82, Q83, Q84]), "scope" : qUnion([Q85])});
        }
        {
            var Q0;
            Q0=sQuery(id+"F2.wireOp",VERTEX,"E3.16.14.0");
            var Q1;
            Q1=sQuery(id+"F2.wireOp",VERTEX,"E3.15.15.0");
            var Q2;
            Q2=sQuery(id+"F2.wireOp",VERTEX,"E3.16.16.0");
            var Q3;
            Q3=sQuery(id+"F2.wireOp",VERTEX,"E3.16.0.0");
            var Q4;
            Q4=sQuery(id+"F2.wireOp",VERTEX,"E3.15.2.0");
            var Q5;
            Q5=sQuery(id+"F2.wireOp",VERTEX,"E3.16.5.0");
            var Q6;
            Q6=sQuery(id+"F2.wireOp",VERTEX,"E3.16.12.0");
            var Q7;
            Q7=sQuery(id+"F2.wireOp",VERTEX,"E3.15.13.0");
            var Q8;
            Q8=sQuery(id+"F2.wireOp",VERTEX,"E3.15.7.0");
            var Q9;
            Q9=sQuery(id+"F2.wireOp",VERTEX,"E3.16.13.0");
            var Q10;
            Q10=sQuery(id+"F2.wireOp",VERTEX,"E3.16.6.0");
            var Q11;
            Q11=sQuery(id+"F2.wireOp",VERTEX,"E3.15.14.0");
            var Q12;
            Q12=sQuery(id+"F2.wireOp",VERTEX,"E3.15.4.0");
            var Q13;
            Q13=sQuery(id+"F2.wireOp",VERTEX,"E3.16.15.0");
            var Q14;
            Q14=sQuery(id+"F2.wireOp",VERTEX,"E3.15.16.0");
            var Q15;
            Q15=sQuery(id+"F2.wireOp",VERTEX,"E3.15.0.0");
            var Q16;
            Q16=sQuery(id+"F2.wireOp",VERTEX,"E3.15.9.0");
            var Q17;
            Q17=sQuery(id+"F2.wireOp",VERTEX,"E3.16.8.0");
            var Q18;
            Q18=sQuery(id+"F2.wireOp",VERTEX,"E3.16.1.0");
            var Q19;
            Q19=sQuery(id+"F2.wireOp",VERTEX,"E3.15.8.0");
            var Q20;
            Q20=sQuery(id+"F2.wireOp",VERTEX,"E3.15.3.0");
            var Q21;
            Q21=sQuery(id+"F2.wireOp",VERTEX,"E3.16.2.0");
            var Q22;
            Q22=sQuery(id+"F2.wireOp",VERTEX,"E3.16.3.0");
            var Q23;
            Q23=sQuery(id+"F2.wireOp",VERTEX,"E3.15.10.0");
            var Q24;
            Q24=sQuery(id+"F2.wireOp",VERTEX,"E3.16.9.0");
            var Q25;
            Q25=sQuery(id+"F2.wireOp",VERTEX,"E3.15.5.0");
            var Q26;
            Q26=sQuery(id+"F2.wireOp",VERTEX,"E3.16.10.0");
            var Q27;
            Q27=sQuery(id+"F2.wireOp",VERTEX,"E3.15.11.0");
            var Q28;
            Q28=sQuery(id+"F2.wireOp",VERTEX,"E3.15.1.0");
            var Q29;
            Q29=sQuery(id+"F2.wireOp",VERTEX,"E3.16.4.0");
            var Q30;
            Q30=sQuery(id+"F2.wireOp",VERTEX,"E3.16.11.0");
            var Q31;
            Q31=sQuery(id+"F2.wireOp",VERTEX,"E3.15.12.0");
            var Q32;
            Q32=sQuery(id+"F2.wireOp",VERTEX,"E3.15.6.0");
            var Q33;
            Q33=sQuery(id+"F2.wireOp",VERTEX,"E3.16.7.0");
            var Q34;
            Q34=makeQuery(id+"F1.opExtrude","SWEPT_BODY",BODY,{"disambiguationData":[OSD([sQuery(id+"F0.wireOp",EDGE,"E0.bottom"),sQuery(id+"F0.wireOp",EDGE,"E0.top"),sQuery(id+"F0.wireOp",EDGE,"E0.left"),sQuery(id+"F0.wireOp",EDGE,"E0.right")])]});
            hole(context, id + "F6", {"style" : HoleStyle.C_BORE, "endStyle" : HoleEndStyle.THROUGH, "holeDiameter" : 7.94 * mm, "cBoreDiameter" : 12.95 * mm, "cBoreDepth" : 1.27 * mm, "isTappedThrough" : true, "tappedDepth" : 12.7 * mm, "tapClearance" : 3, "locations" : qUnion([Q0, Q1, Q2, Q3, Q4, Q5, Q6, Q7, Q8, Q9, Q10, Q11, Q12, Q13, Q14, Q15, Q16, Q17, Q18, Q19, Q20, Q21, Q22, Q23, Q24, Q25, Q26, Q27, Q28, Q29, Q30, Q31, Q32, Q33]), "scope" : qUnion([Q34])});
        }
    });
